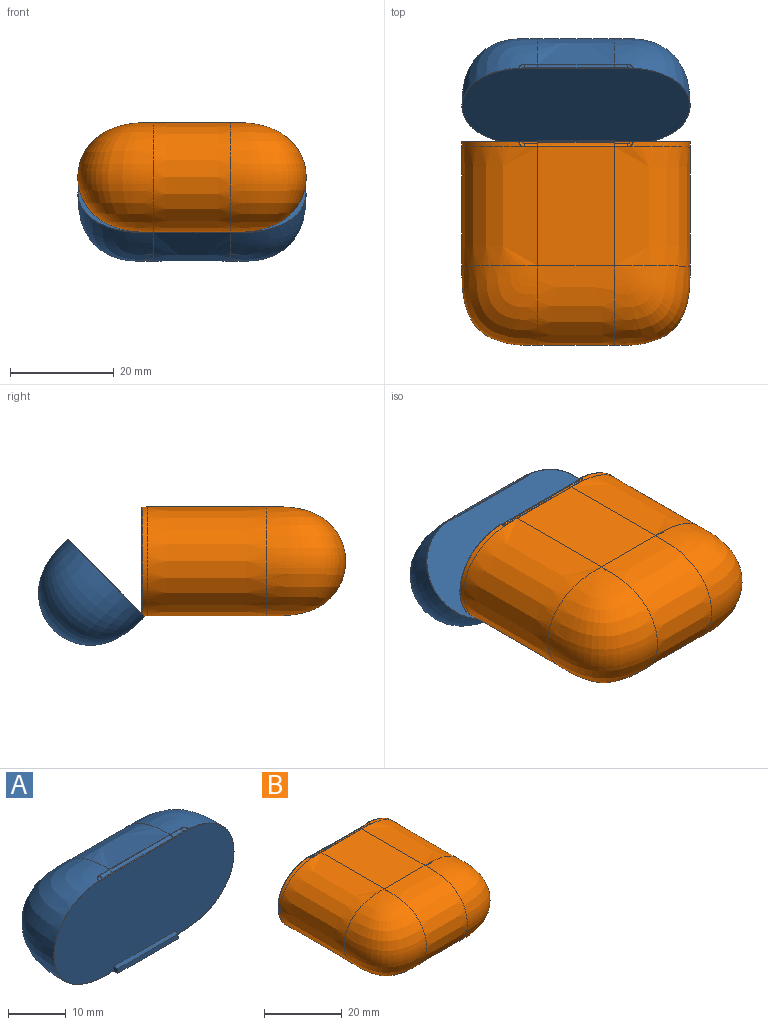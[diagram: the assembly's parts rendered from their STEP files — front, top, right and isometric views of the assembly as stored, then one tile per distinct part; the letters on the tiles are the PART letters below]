
ASSEMBLY  parts=2 mates=1
PART A: 27 faces, bbox 44.6x15.9x21.6 mm
  f0: extruded ~14.82x0.67mm, area 11mm2, adj f1,f2,f5,f12
  f1: bspline ~2.89x0.71mm, area 1.9mm2, adj f0,f3,f5,f13
  f2: bspline ~2.62x0.71mm, area 1.9mm2, adj f0,f4,f5,f11
  f3: bspline ~1.09x1mm, area 0.6mm2, adj f1,f5,f14,f16
  f4: bspline ~1.09x1mm, area 0.6mm2, adj f2,f5,f10,f19
  f5: plane 21.38x0.8mm, normal (0,0,1), area 4.7mm2, adj f0,f1,f2,f3,f4,f18
  f6: bspline ~21.1x15.35mm, area 612.6mm2, adj f7,f10,f11,f20
  f7: extruded ~21.08x14.82mm, area 579.6mm2, adj f6,f8,f12,f22
  f8: bspline ~21.1x15.35mm, area 612.6mm2, adj f7,f13,f14,f17
  f9: plane 44x20.88mm, normal (0,-1,0), area 795mm2, adj f15,f16,f17,f18,f19,f20,f21,f23
  f10: bspline ~1.03x0.97mm, area 0.1mm2, adj f4,f6,f11,f21
  f11: bspline ~3.78x0.1mm, area 0.2mm2, adj f2,f6,f10,f12
  f12: cylinder r=0.1mm len=14.82mm, axis (1,0,0), area 1.2mm2, adj f0,f7,f11,f13
  f13: bspline ~2.59x0.07mm, area 0.2mm2, adj f1,f8,f12,f14
  f14: bspline ~1.03x0.97mm, area 0.1mm2, adj f3,f8,f13,f15
  f15: bspline ~0.09x0.06mm, area 0mm2, adj f9,f14,f16,f17
  f16: bspline ~0.65x0.22mm, area 0mm2, adj f3,f9,f15,f18
  f17: bspline ~21.05x14.76mm, area 2.9mm2, adj f8,f9,f15,f23
  f18: cylinder r=0.05mm len=20.84mm, axis (1,0,0), area 1.6mm2, adj f5,f9,f16,f19
  f19: bspline ~0.71x0.27mm, area 0mm2, adj f4,f9,f18,f21
  f20: bspline ~21.09x14.99mm, area 2.9mm2, adj f6,f9,f21,f25
  f21: bspline ~0.09x0.07mm, area 0mm2, adj f9,f10,f19,f20
  f22: plane 14.82x1.05mm, normal (0,0,-1), area 15.6mm2, adj f7,f23,f25,f26
  f23: plane 1.05x1mm, normal (1,0,0), area 1mm2, adj f9,f17,f22,f24,f26
  f24: plane 14.82x1mm, normal (0,0,1), area 14.8mm2, adj f9,f23,f25,f26
  f25: plane 1.05x1mm, normal (-1,0,0), area 1mm2, adj f9,f20,f22,f24,f26
  f26: plane 14.82x1mm, normal (0,-1,0), area 14.8mm2, adj f22,f23,f24,f25
PART B: 34 faces, bbox 44.5x54.1x21.5 mm
  f0: plane 14.82x0.03mm, normal (0,0,-1), area 0.4mm2, adj f1,f2,f7,f33
  f1: bspline ~21.1x15.35mm, area 35.5mm2, adj f0,f8,f21,f22,f24,f30
  f2: bspline ~21.1x15.35mm, area 35.7mm2, adj f0,f10,f18,f19,f27,f31
  f3: bspline ~21.1x15.35mm, area 336mm2, adj f4,f8
  f4: extruded ~21.1x15.35mm, area 627.3mm2, adj f3,f5,f7,f9
  f5: bspline ~21.1x15.35mm, area 336mm2, adj f4,f10
  f6: plane 14.82x0.01mm, normal (0,0,1), area 0.1mm2, adj f9,f20
  f7: plane 23x14.82mm, normal (0,0,-1), area 340.9mm2, adj f0,f4,f8,f10
  f8: extruded ~23x21.1mm, area 936.1mm2, adj f1,f3,f7,f9
  f9: plane 23x14.82mm, normal (0,0,1), area 341mm2, adj f4,f6,f8,f10
  f10: extruded ~23x21.1mm, area 936.3mm2, adj f2,f5,f7,f9
  f11: plane 21.3x0.72mm, normal (0,0,1), area 4.5mm2, adj f12,f13,f14,f15,f16,f26
  f12: bspline ~1.09x1.01mm, area 0.6mm2, adj f11,f13,f22,f25
  f13: bspline ~2.68x0.71mm, area 1.9mm2, adj f11,f12,f15,f21
  f14: bspline ~1.16x1.1mm, area 0.6mm2, adj f11,f16,f18,f28
  f15: extruded ~14.82x0.69mm, area 11.3mm2, adj f11,f13,f16,f20
  f16: bspline ~2.63x0.71mm, area 1.9mm2, adj f11,f14,f15,f19
  f17: plane 44x20.88mm, normal (0,1,0), area 794.8mm2, adj f23,f24,f25,f26,f27,f28,f29,f30
  f18: bspline ~1.21x1.05mm, area 0.1mm2, adj f2,f14,f19,f29
  f19: bspline ~3.35x0.13mm, area 0.2mm2, adj f2,f16,f18,f20
  f20: bspline ~17.7x0.07mm, area 1.2mm2, adj f6,f15,f19,f21
  f21: bspline ~3.35x0.13mm, area 0.2mm2, adj f1,f13,f20,f22
  f22: bspline ~1.79x1.05mm, area 0.1mm2, adj f1,f12,f21,f23
  f23: bspline ~0.09x0.06mm, area 0mm2, adj f17,f22,f24,f25
  f24: bspline ~21x14.72mm, area 2.9mm2, adj f1,f17,f23,f30
  f25: bspline ~0.68x0.26mm, area 0mm2, adj f12,f17,f23,f26
  f26: cylinder r=0.05mm len=20.86mm, axis (-1,0,0), area 1.6mm2, adj f11,f17,f25,f28
  f27: bspline ~21.08x14.76mm, area 2.9mm2, adj f2,f17,f29,f31
  f28: bspline ~0.69x0.22mm, area 0mm2, adj f14,f17,f26,f29
  f29: bspline ~0.09x0.07mm, area 0mm2, adj f17,f18,f27,f28
  f30: plane 1x1mm, normal (-1,0,0), area 1mm2, adj f1,f17,f24,f32,f33
  f31: plane 1x1mm, normal (1,0,0), area 1mm2, adj f2,f17,f27,f32,f33
  f32: plane 14.82x1mm, normal (0,0,-1), area 14.8mm2, adj f17,f30,f31,f33
  f33: plane 14.82x1mm, normal (0,1,0), area 14.8mm2, adj f0,f30,f31,f32
PLACE A rot(axis=(-1,0,0),44.6deg) t=(-12.68,18.43,10.69)mm
PLACE B t=(-12.68,7.94,5.11)mm fixed
MATE revolute A.f23 <-> B.f30  axis (1,0,0) through (-5.27,19.97,-4.94)mm
